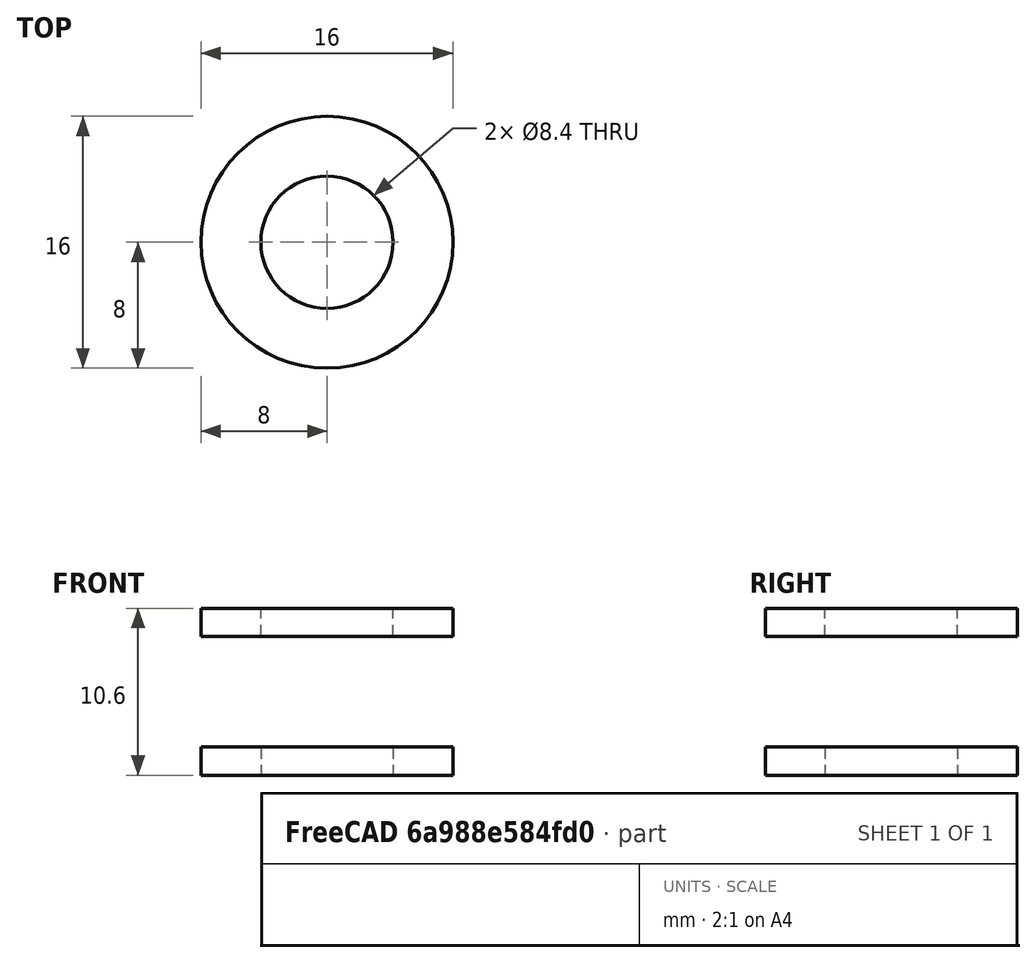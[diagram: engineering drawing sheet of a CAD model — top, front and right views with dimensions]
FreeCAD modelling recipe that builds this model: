
FCSTD DOCUMENT  (FreeCAD 0.20R29177 +426 (Git))
Label: ASM_RollerShaft
License: All rights reserved
LicenseURL: http://en.wikipedia.org/wiki/All_rights_reserved
objects: App::DocumentObjectGroup×4, App::Link×3, Part::FeaturePython×2, PartDesign::CoordinateSystem×1, App::FeaturePython×1, App::Part×1
note: 3 computed .brp shape members not serialized (recipe doc carries the construction recipe); baked Part::Feature solids carry a one-line shape summary decoded from their .brp
EXTERNAL_REF file=Shaft.FCStd obj=LCS_1
EXTERNAL_REF file=Shaft.FCStd obj=Part
EXTERNAL_REF file=Bearing608.FCStd obj=LCS_axle
EXTERNAL_REF file=Bearing608.FCStd obj=Part
EXTERNAL_REF file=TableRollerTire.FCStd obj=LCS_Origin
EXTERNAL_REF file=TableRollerTire.FCStd obj=Assembly
EXTERNAL_REF file=Bearing608.FCStd obj=Chamfer

FEATURE [App::DocumentObjectGroup] Parts
FEATURE [PartDesign::CoordinateSystem] LCS_Origin
  AttacherType = Attacher::AttachEngine3D
  MapMode = 2
  Support = -> [X_Axis]
FEATURE [App::FeaturePython] Variables  # WARN: FeaturePython — macro-defined, semantics opaque (R4)
  Type = App::PropertyContainer
FEATURE [App::DocumentObjectGroup] Constraints
FEATURE [App::DocumentObjectGroup] Configurations
FEATURE [App::Link] DowelPin
  AssemblyType = Part::Link
  AttachedBy = #LCS_1
  AttachedTo = Parent Assembly#LCS_Origin
  LinkedObject = -> <external Shaft.FCStd>#Part
  SolverId = Asm4EE
  expr: Placement = LCS_Origin.Placement * AttachmentOffset * Shaft#LCS_1.Placement ^ -1
FEATURE [App::Link] Bearing608
  AssemblyType = Part::Link
  AttachedBy = #LCS_axle
  AttachedTo = DowelPin#LCS_1
  LinkedObject = -> <external Bearing608.FCStd>#Part
  SolverId = Asm4EE
  expr: Placement = DowelPin.Placement * Shaft#LCS_1.Placement * AttachmentOffset * Bearing608#LCS_axle.Placement ^ -1
FEATURE [App::Link] TableRollerTire
  AttachedBy = #LCS_Origin
  AttachedTo = Bearing608#LCS_axle
  LinkedObject = -> <external TableRollerTire.FCStd>#Assembly
  SolverId = Asm4EE
  expr: Placement = Bearing608.Placement * Bearing608#LCS_axle.Placement * AttachmentOffset * TableRollerTire#LCS_Origin.Placement ^ -1
FEATURE [Part::FeaturePython] Washer  label="M8-Washer"  # Fasteners workbench fastener (typed FeaturePython)
  Placement = pos=(0,-1e-15,-3.5) rot=(1,0,0;3.14159rad)
  baseObject = -> <external Bearing608.FCStd>#Chamfer [Edge11]
  diameter = 8
  invert = false
  matchOuter = true
  offset = 0
  type = 3
FEATURE [Part::FeaturePython] Washer001  label="M8-Washer001"  # Fasteners workbench fastener (typed FeaturePython)
  Placement = pos=(0,1e-15,3.5) rot=(0,0,1;0rad)
  baseObject = -> <external Bearing608.FCStd>#Chamfer [Edge1]
  diameter = 8
  invert = true
  matchOuter = true
  offset = 0
  type = 3
FEATURE [App::DocumentObjectGroup] Fasteners
  Group = -> [Washer,Washer001]
FEATURE [App::Part] Assembly
  AssemblyType = Part::Link
  Group = -> [LCS_Origin,Variables,Constraints,Configurations,DowelPin,Bearing608,Fasteners,TableRollerTire,Washer,Washer001]
  Origin = -> Origin
  Type = Assembly

RESOLVED EXTERNAL PARTS (link-assembly join: the EXTERNAL_REF files above that resolve inside this repo's crawl, each included once):
---- part Bearing608.FCStd = doc fcstd_2dd5ca27958f ----
FCSTD DOCUMENT  (FreeCAD 0.20R29177 +426 (Git))
Label: Bearing608
License: All rights reserved
LicenseURL: http://en.wikipedia.org/wiki/All_rights_reserved
objects: Sketcher::SketchObject×1, PartDesign::Revolution×1, PartDesign::Chamfer×1, PartDesign::CoordinateSystem×1, App::Part×1
note: 6 computed .brp shape members not serialized (recipe doc carries the construction recipe); baked Part::Feature solids carry a one-line shape summary decoded from their .brp

FEATURE [Sketcher::SketchObject] Sketch
  FullyConstrained = true
  MapMode = 5
  Placement = pos=(0,0,0) rot=(1,0,0;1.5708rad)
  Support = -> [XZ_Plane]
  sketch-geometry (12):
    g0: LineSegment StartX=4 StartY=-3.5 StartZ=0 EndX=5.75 EndY=-3.5 EndZ=0
    g1: LineSegment StartX=11 StartY=-3.5 StartZ=0 EndX=11 EndY=3.5 EndZ=0
    g2: LineSegment StartX=11 StartY=3.5 StartZ=0 EndX=9.25 EndY=3.5 EndZ=0
    g3: LineSegment StartX=4 StartY=3.5 StartZ=0 EndX=4 EndY=-3.5 EndZ=0
    g4: LineSegment StartX=5.75 StartY=3.5 StartZ=0 EndX=6 EndY=3.25 EndZ=0
    g5: LineSegment StartX=6 StartY=3.25 StartZ=0 EndX=9 EndY=3.25 EndZ=0
    g6: LineSegment StartX=9 StartY=3.25 StartZ=0 EndX=9.25 EndY=3.5 EndZ=0
    g7: LineSegment StartX=5.75 StartY=-3.5 StartZ=0 EndX=6 EndY=-3.25 EndZ=0
    g8: LineSegment StartX=6 StartY=-3.25 StartZ=0 EndX=9 EndY=-3.25 EndZ=0
    g9: LineSegment StartX=9 StartY=-3.25 StartZ=0 EndX=9.25 EndY=-3.5 EndZ=0
    g10: LineSegment StartX=5.75 StartY=3.5 StartZ=0 EndX=4 EndY=3.5 EndZ=0
    g11: LineSegment StartX=9.25 StartY=-3.5 StartZ=0 EndX=11 EndY=-3.5 EndZ=0
  constraints (33):
    c: Coincident(g11,g1)
    c: Coincident(g1,g2)
    c: Coincident(g10,g3)
    c: Coincident(g3,g0)
    c: Horizontal(g0)
    c: Horizontal(g2)
    c: Vertical(g1)
    c: DistanceY(g1) = 7
    c: DistanceX(g0) = 4
    c: DistanceX(g11) = 11
    c: Coincident(g4,g5)
    c: Horizontal(g5)
    c: Coincident(g5,g6)
    c: Coincident(g7,g8)
    c: Horizontal(g8)
    c: Coincident(g8,g9)
    c: Coincident(g2,g6)
    c: Coincident(g10,g4)
    c: Tangent(g2,g10)
    c: Coincident(g0,g7)
    c: Coincident(g11,g9)
    c: Tangent(g0,g11)
    c: Equal(g4,g6)
    c: Equal(g6,g7)
    c: Angle(g10,g4) = 2.35619
    c: DistanceX(g2) = -1.75
    c: DistanceX(g10) = -1.75
    c: Equal(g0,g10)
    c: Equal(g11,g2)
    c: Equal(g9,g7)
    c: Parallel(g9,g4)
    c: DistanceY(g5,g1) = 0.25
    c: Symmetric(g0,g3,g-1)
FEATURE [PartDesign::Revolution] Revolution
  AllowMultiFace = false
  Angle = 360
  Axis = (0,-2e-16,1)
  Base = (0,0,0)
  Placement = pos=(0,0,0) rot=(1,0,0;1.5708rad)
  Profile = -> Sketch
  ReferenceAxis = -> Sketch [V_Axis]
  Reversed = true
FEATURE [PartDesign::Chamfer] Chamfer
  Angle = 45
  Base = -> Revolution [Edge3,Edge2,Edge11,Edge12]
  ChamferType = 0
  FlipDirection = false
  Placement = pos=(0,0,0) rot=(1,0,0;1.5708rad)
  Size = 0.25
  Size2 = 1
  SupportTransform = false
  UseAllEdges = false
FEATURE [PartDesign::CoordinateSystem] LCS_axle
  AttacherType = Attacher::AttachEngine3D
  MapMode = 2
  Support = -> [XY_Plane]
FEATURE [App::Part] Part
  Group = -> [Sketch,Revolution,Chamfer,LCS_axle]
  Origin = -> Origin
---- part Shaft.FCStd = doc fcstd_331eed658d49 ----
FCSTD DOCUMENT  (FreeCAD 0.20R29177 +426 (Git))
Label: Shaft
License: All rights reserved
LicenseURL: http://en.wikipedia.org/wiki/All_rights_reserved
objects: Sketcher::SketchObject×1, PartDesign::Pad×1, PartDesign::Chamfer×1, PartDesign::Body×1, App::FeaturePython×1, PartDesign::CoordinateSystem×1, App::Part×1
note: 7 computed .brp shape members not serialized (recipe doc carries the construction recipe); baked Part::Feature solids carry a one-line shape summary decoded from their .brp

FEATURE [Sketcher::SketchObject] Sketch
  FullyConstrained = true
  MapMode = 5
  Support = -> [XY_Plane]
  expr: Constraints[1] = <<Variables>>.Diameter
  sketch-geometry (1):
    g0: Circle CenterX=0 CenterY=0 CenterZ=0 NormalX=0 NormalY=0 NormalZ=1 AngleXU=0 Radius=4
  constraints (2):
    c: Coincident(g0,g-1)
    c: Diameter(g0) = 8
FEATURE [PartDesign::Pad] Pad
  Direction = (0,0,1)
  Length = 20
  Length2 = 10
  Midplane = true
  Profile = -> Sketch
  ReferenceAxis = -> Sketch [N_Axis]
  Type = 0
  expr: Length = <<Variables>>.Length
FEATURE [PartDesign::Chamfer] Chamfer
  Angle = 45
  Base = -> Pad [Edge2,Edge3]
  BaseFeature = -> Pad
  ChamferType = 0
  FlipDirection = false
  Size = 0.4
  Size2 = 1
  SupportTransform = false
  UseAllEdges = false
  expr: Size = <<Variables>>.Diameter * 0.05
FEATURE [PartDesign::Body] Body  label="Shaft001"
  Group = -> [Sketch,Pad,Chamfer]
  Origin = -> Origin
  Tip = -> Chamfer
FEATURE [App::FeaturePython] Variables  # WARN: FeaturePython — macro-defined, semantics opaque (R4)
  Diameter = 8
  Length = 20
  Type = App::PropertyContainer
FEATURE [PartDesign::CoordinateSystem] LCS_1
  AttacherType = Attacher::AttachEngine3D
  MapMode = 2
  Support = -> [XY_Plane001]
FEATURE [App::Part] Part
  Group = -> [Variables,Body,LCS_1]
  LabelDocUser = Shaft
  LabelPartUser = Part
  Origin = -> Origin001
  PadLengthUser = 20.0 
  ShapeLengthUser = 25.1327
  ShapeVolumeUser = 20.0 mm x 7.993 mm x 7.986 mm
  Type = Asm4::VariantLink
---- part TableRollerTire.FCStd = doc fcstd_fe39aaaf2d06 ----
FCSTD DOCUMENT  (FreeCAD 0.20R29177 +426 (Git))
Label: TableRollerTire
License: All rights reserved
LicenseURL: http://en.wikipedia.org/wiki/All_rights_reserved
objects: App::DocumentObjectGroup×3, PartDesign::CoordinateSystem×1, App::FeaturePython×1, Sketcher::SketchObject×1, PartDesign::Revolution×1, PartDesign::Body×1, App::Part×1
note: 5 computed .brp shape members not serialized (recipe doc carries the construction recipe); baked Part::Feature solids carry a one-line shape summary decoded from their .brp

FEATURE [App::DocumentObjectGroup] Parts
FEATURE [PartDesign::CoordinateSystem] LCS_Origin
  AttacherType = Attacher::AttachEngine3D
  MapMode = 2
  Support = -> [X_Axis]
FEATURE [App::FeaturePython] Variables  # WARN: FeaturePython — macro-defined, semantics opaque (R4)
  Type = App::PropertyContainer
FEATURE [App::DocumentObjectGroup] Constraints
FEATURE [App::DocumentObjectGroup] Configurations
FEATURE [Sketcher::SketchObject] Sketch
  FullyConstrained = true
  MapMode = 5
  Placement = pos=(0,0,0) rot=(1,0,0;1.5708rad)
  Support = -> [XZ_Plane001]
  sketch-geometry (11):
    g0: LineSegment StartX=9.9 StartY=4.25 StartZ=0 EndX=9.9 EndY=-4.25 EndZ=0
    g1: ArcOfCircle CenterX=12 CenterY=0 CenterZ=0 NormalX=0 NormalY=0 NormalZ=1 AngleXU=0 Radius=3 StartAngle=5.47627 EndAngle=7.0901
    g2: LineSegment StartX=14.0752 StartY=2.16647 StartZ=0 EndX=11.9 EndY=4.25 EndZ=0
    g3: LineSegment StartX=14.0752 StartY=-2.16647 StartZ=0 EndX=11.9 EndY=-4.25 EndZ=0
    g4: LineSegment StartX=11.9 StartY=-4.25 StartZ=0 EndX=9.9 EndY=-4.25 EndZ=0
    g5: LineSegment StartX=11.9 StartY=4.25 StartZ=0 EndX=9.9 EndY=4.25 EndZ=0
    g6: GeomPoint X=15 Y=0 Z=0
    g7: LineSegment StartX=10.9 StartY=0 StartZ=0 EndX=10.9 EndY=3.25 EndZ=0
    g8: LineSegment StartX=10.9 StartY=0 StartZ=0 EndX=10.9 EndY=-3.25 EndZ=0
    g9: LineSegment StartX=9.9 StartY=4.25 StartZ=0 EndX=10.9 EndY=3.25 EndZ=0
    g10: LineSegment StartX=10.9 StartY=-3.25 StartZ=0 EndX=9.9 EndY=-4.25 EndZ=0
  constraints (30):
    c: Vertical(g0)
    c: PointOnObject(g1,g-1)
    c: Radius(g1) = 3
    c: DistanceY(g0,g0) = 8.5
    c: Tangent(g2,g1) = -1.5708
    c: Coincident(g4,g3)
    c: Horizontal(g4)
    c: Tangent(g3,g1) = 1.5708
    c: Coincident(g5,g2)
    c: Horizontal(g5)
    c: Coincident(g5,g0)
    c: Coincident(g4,g0)
    c: Equal(g4,g5)
    c: DistanceX(g5,g5) = 2
    c: PointOnObject(g6,g1)
    c: PointOnObject(g6,g-1)
    c: DistanceX(g-1,g6) = 15
    c: PointOnObject(g7,g-1)
    c: Vertical(g7)
    c: Coincident(g8,g7)
    c: Vertical(g8)
    c: Equal(g8,g7)
    c: DistanceY(g8,g7) = 6.5
    c: Coincident(g9,g5)
    c: Coincident(g9,g7)
    c: Coincident(g10,g8)
    c: Coincident(g10,g4)
    c: Equal(g10,g9)
    c: Angle(g9,g-1) = 0.785398
    c: DistanceX(g-1,g7) = 10.9
FEATURE [PartDesign::Revolution] Revolution
  Angle = 360
  Axis = (0,-2e-16,1)
  Base = (0,0,0)
  Placement = pos=(0,0,0) rot=(1,0,0;1.5708rad)
  Profile = -> Sketch
  ReferenceAxis = -> Sketch [V_Axis]
  Reversed = true
FEATURE [PartDesign::Body] Body
  Group = -> [Sketch,Revolution]
  Origin = -> Origin001
  Tip = -> Revolution
FEATURE [App::Part] Assembly
  AssemblyType = Part::Link
  Group = -> [LCS_Origin,Variables,Constraints,Configurations,Body]
  Origin = -> Origin
  Type = Assembly
